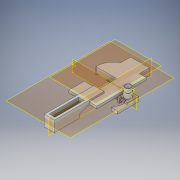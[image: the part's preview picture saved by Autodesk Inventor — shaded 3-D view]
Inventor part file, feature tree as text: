
AUTODESK INVENTOR PART (.ipt)
format: ipt  version: 2018 (Build 220112000, 112)  size: 546,816 bytes
history: native  units: in
note: dims shown in document units (in); Inventor stores cm internally (conversion verified against a paired STEP export)
features: sketch x48, extrude x44, plane x6, loft x1, other x1
ambient origin geometry x8: Origin, YZ Plane, XZ Plane, XY Plane, X Axis, Y Axis, Z Axis, Center Point
bodies: Solid1 (feature_tree)
feature tree (100):
  extrude  "Extrusion1"  Depth=1.9654in
  extrude  "Extrusion2"  Depth=1.3606in
  extrude  "Extrusion3"  Depth=0.1673in TaperAngle=0.0deg
  extrude  "Extrusion4"  Depth=0.3543in
  extrude  "Extrusion5"  Depth=0.3972in TaperAngle=0.0deg
  extrude  "Extrusion6"  Depth=0.3972in TaperAngle=0.0deg
  extrude  "Extrusion7"  Depth=0.161in TaperAngle=0.0deg
  extrude  "Extrusion8"  Depth=0.4331in
  extrude  "Extrusion9"  Depth=1.378in
  extrude  "Extrusion10"  Depth=1.5748in TaperAngle=0.0deg
  extrude  "Extrusion11"  Depth=0.0787in TaperAngle=0.0deg
  extrude  "Extrusion12"  Depth=0.3937in TaperAngle=0.0deg
  extrude  "Extrusion13"  Depth=0.2398in
  extrude  "Extrusion14"  Depth=0.0984in TaperAngle=0.0deg
  extrude  "Extrusion15"  TaperAngle=90.0deg  [1 undecoded]
  sketch  "Sketch18"  dims[d50=0.0in d51=90.0deg d52=0.0in d53=90.0deg]
  plane  "Work Plane1"
  sketch  "Sketch19"  dims[d54=0.1181in d55=0.3937in d56=0.0in]
  sketch  "Sketch20"  dims[d57=0.0787in d58=0.1181in]
  loft  "Loft1"
  extrude  "Extrusion16"  Depth=0.3937in TaperAngle=0.0deg
  extrude  "Extrusion17"  Depth=0.1181in
  extrude  "Extrusion18"  Depth=0.0394in
  extrude  "Extrusion19"  Depth=0.0689in TaperAngle=0.0deg
  extrude  "Extrusion20"  Depth=0.0689in TaperAngle=0.0deg
  extrude  "Extrusion21"  Depth=0.0472in TaperAngle=0.0deg
  extrude  "Extrusion22"  Depth=0.0472in TaperAngle=0.0deg
  extrude  "Extrusion23"  Depth=0.3555in
  extrude  "Extrusion24"  Depth=0.1575in TaperAngle=0.0deg
  extrude  "Extrusion25"  Depth=0.2756in TaperAngle=0.0deg
  extrude  "Extrusion26"  Depth=0.1575in TaperAngle=0.0deg
  extrude  "Extrusion27"  Depth=0.5118in TaperAngle=0.0deg
  extrude  "Extrusion28"  Depth=0.0394in TaperAngle=0.0deg
  extrude  "Extrusion29"  Depth=0.2756in TaperAngle=0.0deg
  extrude  "Extrusion30"  Depth=0.3937in TaperAngle=0.0deg
  extrude  "Extrusion31"  Depth=0.315in TaperAngle=0.0deg
  extrude  "Extrusion32"  Depth=0.7874in TaperAngle=0.0deg
  extrude  "Extrusion33"  Depth=0.0787in TaperAngle=0.0deg
  plane  "Work Plane2"
  sketch  "Sketch40"  dims[d127=0.2165in d128=0.0in d129=0.5906in d130=0.0in]
  sketch  "Sketch41"
  extrude  "Extrusion34"  Depth=0.2756in TaperAngle=0.0deg
  plane  "Work Plane3"
  extrude  "Extrusion35"  Depth=0.5906in TaperAngle=0.0deg
  plane  "Work Plane4"
  extrude  "Extrusion36"  [1 undecoded]
  plane  "Work Plane5"
  extrude  "Extrusion37"  Depth=0.5906in TaperAngle=0.0deg
  extrude  "Extrusion40"  [1 undecoded]
  extrude  "Extrusion41"  [1 undecoded]
  extrude  "Extrusion42"  [1 undecoded]
  extrude  "Extrusion43"  [1 undecoded]
  extrude  "Extrusion44"  [1 undecoded]
  plane  "Work Plane6"
  extrude  "Extrusion45"  [1 undecoded]
  extrude  "Extrusion46"  [1 undecoded]
  sketch  "Sketch1"  dims[d0=1.9102in d1=1.9654in]
  sketch  "Sketch2"  dims[d2=0.0984in d3=0.0in d4=1.3606in]
  sketch  "Sketch3"  dims[d5=0.7315in d6=0.1673in d7=0.0in]
  sketch  "Sketch4"  dims[d8=0.1969in d9=0.3543in]
  sketch  "Sketch5"  dims[d10=0.265in d11=0.0in d12=0.3972in d13=0.0in]
  sketch  "Sketch6"  dims[d14=0.1772in d15=0.3972in d16=0.0in]
  sketch  "Sketch7"  dims[d19=0.228in d20=0.161in d21=0.0in]
  sketch  "Sketch8"  dims[d22=0.4016in d23=0.4331in]
  sketch  "Sketch10"  dims[d24=1.378in d25=0.0in d26=0.1654in]
  sketch  "Sketch11"  dims[d27=1.1417in d28=1.5748in d29=0.0in]
  sketch  "Sketch13"  dims[d30=0.1772in d31=0.0787in d32=0.0in]
  sketch  "Sketch14"  dims[d33=0.3937in d34=0.0in d38=0.1181in d39=0.0in]
  sketch  "Sketch15"  dims[d40=0.1181in d41=0.0in d42=0.2398in]
  sketch  "Sketch16"  dims[d43=0.0787in d44=0.0in d45=0.0984in d46=0.0in]
  sketch  "Sketch17"  dims[d47=0.1496in d48=0.0in d49=90.0deg]
  sketch  "Sketch21"  dims[d59=0.0787in d60=0.0in d61=0.0394in]
  other  "Edges1"
  sketch  "Sketch22"  dims[d62=0.0394in d63=0.0689in d64=0.0in]
  sketch  "Sketch23"  dims[d65=0.0394in d66=0.0689in d67=0.0in]
  sketch  "Sketch24"  dims[d68=0.0197in d69=0.0472in d70=0.0in]
  sketch  "Sketch25"  dims[d71=0.0197in d72=0.0472in d73=0.0in]
  sketch  "Sketch26"  dims[d74=0.3555in d75=0.0in d76=0.3555in]
  sketch  "Sketch27"  dims[d77=0.1575in d78=0.0in d79=0.0984in d80=0.0in]
  sketch  "Sketch28"  dims[d81=0.2756in d82=0.0984in d83=0.0in]
  sketch  "Sketch29"  dims[d84=0.1575in d85=0.0787in d86=0.0in]
  sketch  "Sketch30"  dims[d87=0.0295in d88=0.5118in d89=0.0in]
  sketch  "Sketch31"  dims[d90=0.0394in d91=0.0in d92=0.0394in d93=0.0in]
  sketch  "Sketch32"  dims[d94=0.2756in d95=0.0in d96=0.5906in d97=0.0in]
  sketch  "Sketch33"  dims[d98=0.3937in d99=0.0in d100=0.0787in d101=0.0in]
  sketch  "Sketch34"  dims[d102=0.1841in d103=0.315in d104=0.0in]
  sketch  "Sketch35"  dims[d105=1.5748in d106=0.0in d107=0.7874in d108=0.0in]
  sketch  "Sketch36"  dims[d109=0.0in d110=0.0787in d111=0.0in]
  sketch  "Sketch37"  dims[d116=0.3937in d117=0.0in d118=0.2756in d119=0.0in]
  sketch  "Sketch38"  dims[d120=0.1181in d121=0.0in d122=0.5906in d123=0.0in]
  sketch  "Sketch39"  dims[d124=0.3976in d125=0.0in d126=-0.0787in]
  sketch  "Sketch42"
  sketch  "Sketch44"
  sketch  "Sketch45"
  sketch  "Sketch46"
  sketch  "Sketch47"
  sketch  "Sketch48"
  sketch  "Sketch49"
  sketch  "Sketch50"
  sketch  "Sketch51"
note: 9 required parameter values undecoded (feature->parameter linkage not recoverable at this tier; creation-order binding heuristic only, values carry confidence <= 0.55)
